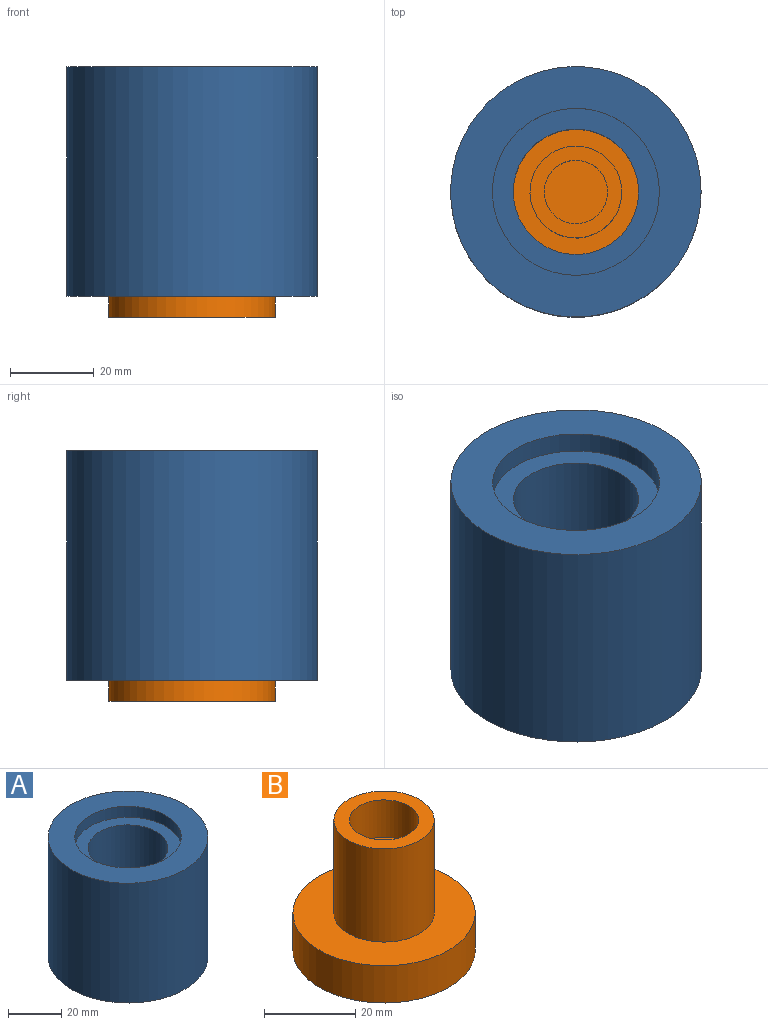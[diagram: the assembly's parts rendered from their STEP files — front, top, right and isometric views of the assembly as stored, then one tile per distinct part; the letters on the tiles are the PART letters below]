
ASSEMBLY  parts=2 mates=1
PART A: 8 faces, bbox 60x60x55 mm
  f0: plane 40x40mm, normal (0,0,-1), area 549.8mm2, adj f2,f6
  f1: plane 40x40mm, normal (0,0,1), area 549.8mm2, adj f2,f4
  f2: cylinder r=15mm len=45mm, axis (0,0,-1), area 4241.2mm2, adj f0,f1
  f3: cylinder r=30mm len=60mm, axis (0,0,-1), area 10367.3mm2, adj f5,f7
  f4: cylinder r=20mm len=40mm, axis (0,0,-1), area 628.3mm2, adj f1,f5
  f5: plane 60x60mm, normal (0,0,1), area 1570.8mm2, adj f3,f4
  f6: cylinder r=20mm len=40mm, axis (0,0,1), area 628.3mm2, adj f0,f7
  f7: plane 60x60mm, normal (0,0,-1), area 1570.8mm2, adj f3,f6
PART B: 7 faces, bbox 40x40x35 mm
  f0: cylinder r=19.98mm len=39.96mm, axis (0,0,-1), area 1255.4mm2, adj f1,f2
  f1: plane 39.96x39.96mm, normal (0,0,1), area 874mm2, adj f0,f3
  f2: plane 39.96x39.96mm, normal (0,0,-1), area 1254.1mm2, adj f0
  f3: cylinder r=11mm len=25mm, axis (0,0,-1), area 1727.9mm2, adj f1,f5
  f4: cylinder r=7.6mm len=15.2mm, axis (0,0,-1), area 477.5mm2, adj f5,f6
  f5: plane 22x22mm, normal (0,0,1), area 198.7mm2, adj f3,f4
  f6: plane 15.2x15.2mm, normal (0,0,1), area 181.5mm2, adj f4
PLACE A t=(-24.35,2.32,2.27)mm fixed
PLACE B rot(axis=(0,0,1),33.3deg) t=(-24.35,2.32,-7.73)mm
MATE revolute B.f0 <-> A.f2  axis (0,0,1) through (-24.35,2.32,2.27)mm
